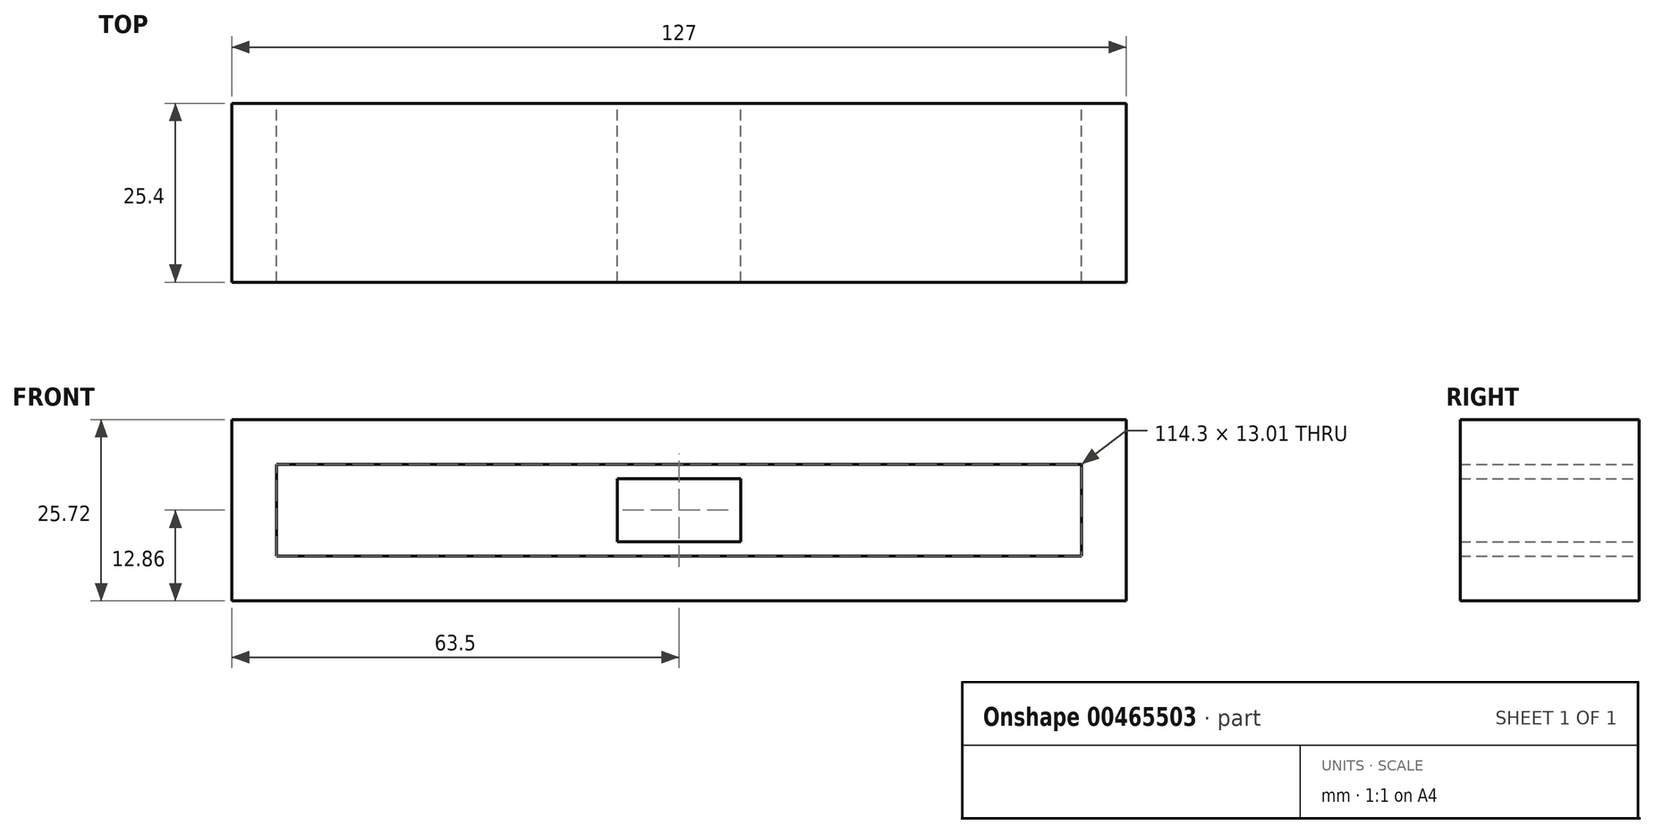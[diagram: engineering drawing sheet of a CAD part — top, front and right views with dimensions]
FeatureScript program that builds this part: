
annotation { "Feature Type Name" : "Feature", "Feature Type Description" : "" }
export const myFeature = defineFeature(function(context is Context, id is Id, definition is map)
    precondition{}
    {
        {
            var Q0;
            Q0=qCreatedBy(makeId("Front.planeOp"),FACE);
            var sketch = newSketch(context, id + "F0", { "sketchPlane" : qUnion([Q0])});
            skLineSegment(sketch, "E0.bottom", {"start": v(63.5, 12.86) * mm, "end": v(-63.5, 12.86) * mm});
            skLineSegment(sketch, "E0.top", {"start": v(63.5, -12.86) * mm, "end": v(-63.5, -12.86) * mm});
            skLineSegment(sketch, "E0.left", {"start": v(63.5, 12.86) * mm, "end": v(63.5, -12.86) * mm});
            skLineSegment(sketch, "E0.right", {"start": v(-63.5, 12.86) * mm, "end": v(-63.5, -12.86) * mm});
            skPoint(sketch, "E0.middle", {"position": v(0, 0) * mm});
            skLineSegment(sketch, "E1.bottom", {"start": v(57.15, 6.5) * mm, "end": v(-57.15, 6.5) * mm});
            skLineSegment(sketch, "E1.top", {"start": v(57.15, -6.5) * mm, "end": v(-57.15, -6.5) * mm});
            skLineSegment(sketch, "E1.left", {"start": v(57.15, 6.5) * mm, "end": v(57.15, -6.5) * mm});
            skLineSegment(sketch, "E1.right", {"start": v(-57.15, 6.5) * mm, "end": v(-57.15, -6.5) * mm});
            skSolve(sketch);
        }
        {
            var Q0;
            Q0=makeQuery(id+"F0.imprint","IMPRINT",FACE,{"disambiguationData":[TD([[makeQuery(id+"F0.imprint","IMPRINT",EDGE,{"derivedFrom":sQuery(id+"F0.wireOp",EDGE,"E0.bottom")}),1.0]])]});
            extrude(context, id + "F1", {"entities" : qUnion([Q0]), "depth" : 25.4 * mm});
        }
        {
            var Q0;
            Q0=qCreatedBy(makeId("Front.planeOp"),FACE);
            var sketch = newSketch(context, id + "F2", { "sketchPlane" : qUnion([Q0])});
            skLineSegment(sketch, "E2.bottom", {"start": v(8.77, 4.5) * mm, "end": v(-8.77, 4.5) * mm});
            skLineSegment(sketch, "E2.top", {"start": v(8.77, -4.5) * mm, "end": v(-8.77, -4.5) * mm});
            skLineSegment(sketch, "E2.left", {"start": v(8.77, 4.5) * mm, "end": v(8.77, -4.5) * mm});
            skLineSegment(sketch, "E2.right", {"start": v(-8.77, 4.5) * mm, "end": v(-8.77, -4.5) * mm});
            skPoint(sketch, "E2.middle", {"position": v(0, 0) * mm});
            skSolve(sketch);
        }
        {
            var Q0;
            Q0 = qSketchRegion(id + "F2", true);
            extrude(context, id + "F3", {"entities" : qUnion([Q0]), "depth" : 25.4 * mm, "offsetDistance" : 25.4 * mm});
        }
    });
